# Revit family: RVT_MACOM_CBHT-DN-DG 03 23 A
name_source: partatom
category: Specialty Equipment
units: mm (PartAtom-declared; Revit-internal decimal feet)

## family parameters
Always vertical = Yes
Cut with Voids When Loaded = No
OmniClass Number = 23.40.40.14.17.21
OmniClass Title = Grills
Part Type = Normal
Room Calculation Point = No
Round Connector Dimension = Use Diameter
Shared = No
Work Plane-Based = No

## types (2) — shared parameters
Default Elevation = 0 mm
Gas Pressure GLP = 0,0 bar
Gas Pressure GN = 0,0 bar
Manufacturer = MACOM
URL = https://www.acosmacom.com.br
Volume = 0,77 m³

## per-type parameters (varying)
| type | Description | Gas Flow GLP | Gas Flow GN | Gas Input GLP | Gas Input GN |
| CBHT-DN | CHAR-BROILER MACOM HIGH POWER 1006x819x911 mm |  | 3,3 m³/h | 0 Btu/h | 31150 Kcal/h |
| CBHT-DG | CHAR-BROILER MACOM HIGH POWER 1006X819X911 mm | 2,34 Kg/h | 0,0 m³/h | 123200 Btu/h |  |

note: column(s) folded — value = type name in every type: Model

## geometry (parser evidence)
native form markers: Sweep x6
no freeform markers — native parametric forms only
